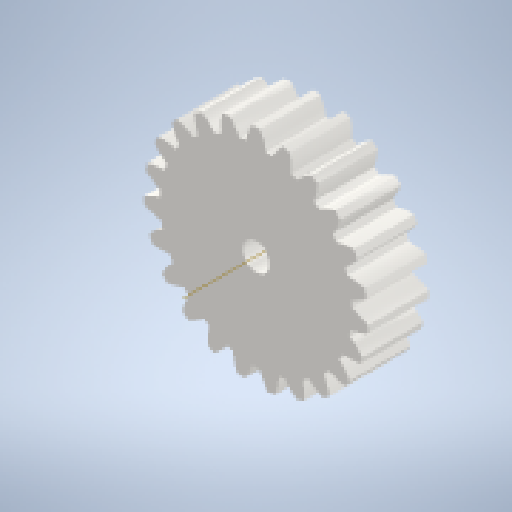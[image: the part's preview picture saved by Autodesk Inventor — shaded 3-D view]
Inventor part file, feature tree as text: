
AUTODESK INVENTOR PART (.ipt)
format: ipt  version: 2023 (Build 270158000, 158)  size: 422,912 bytes
history: native  units: mm (DEFAULTED — no unit token found)
features: other x4, plane x3, sketch x2, extrude x1, hole x1
ambient origin geometry x8: Origin, YZ Plane, XZ Plane, XY Plane, X Axis, Y Axis, Z Axis, Center Point
bodies: Solid1 (feature_tree)
feature tree (11):
  extrude  "Extrusion1"  Depth=10.0mm TaperAngle=0.0deg
  plane  "Work Plane2"
  plane  "Work Plane8"
  plane  "Work Plane9"
  other  "Spur Gear"
  hole  "Hole1"  [1 undecoded]
  other  "Work Axis1"
  sketch  "Sketch1"  dims[d0=36.87672mm d1=10.0mm d2=0.0mm]
  sketch  "Sketch2"  dims[d3=31.625mm d4=10.0mm d5=0.0mm d16=50.0mm d17=0.0mm d34=1.36591mm d39=0.0mm d41=0.0mm d43=50.0mm d46=50.0mm d47=0.0mm d48=0.0mm d60=10.0mm d61=10.0mm d51=4.5mm d52=6.0mm d53=4.0mm d54=2.0mm d55=90.0deg d56=8.0mm d57=20.594885mm]
  other  "Srf1"
  other  "Pitch Diameter"
note: 1 required parameter value undecoded (feature->parameter linkage not recoverable at this tier; creation-order binding heuristic only, values carry confidence <= 0.55)
